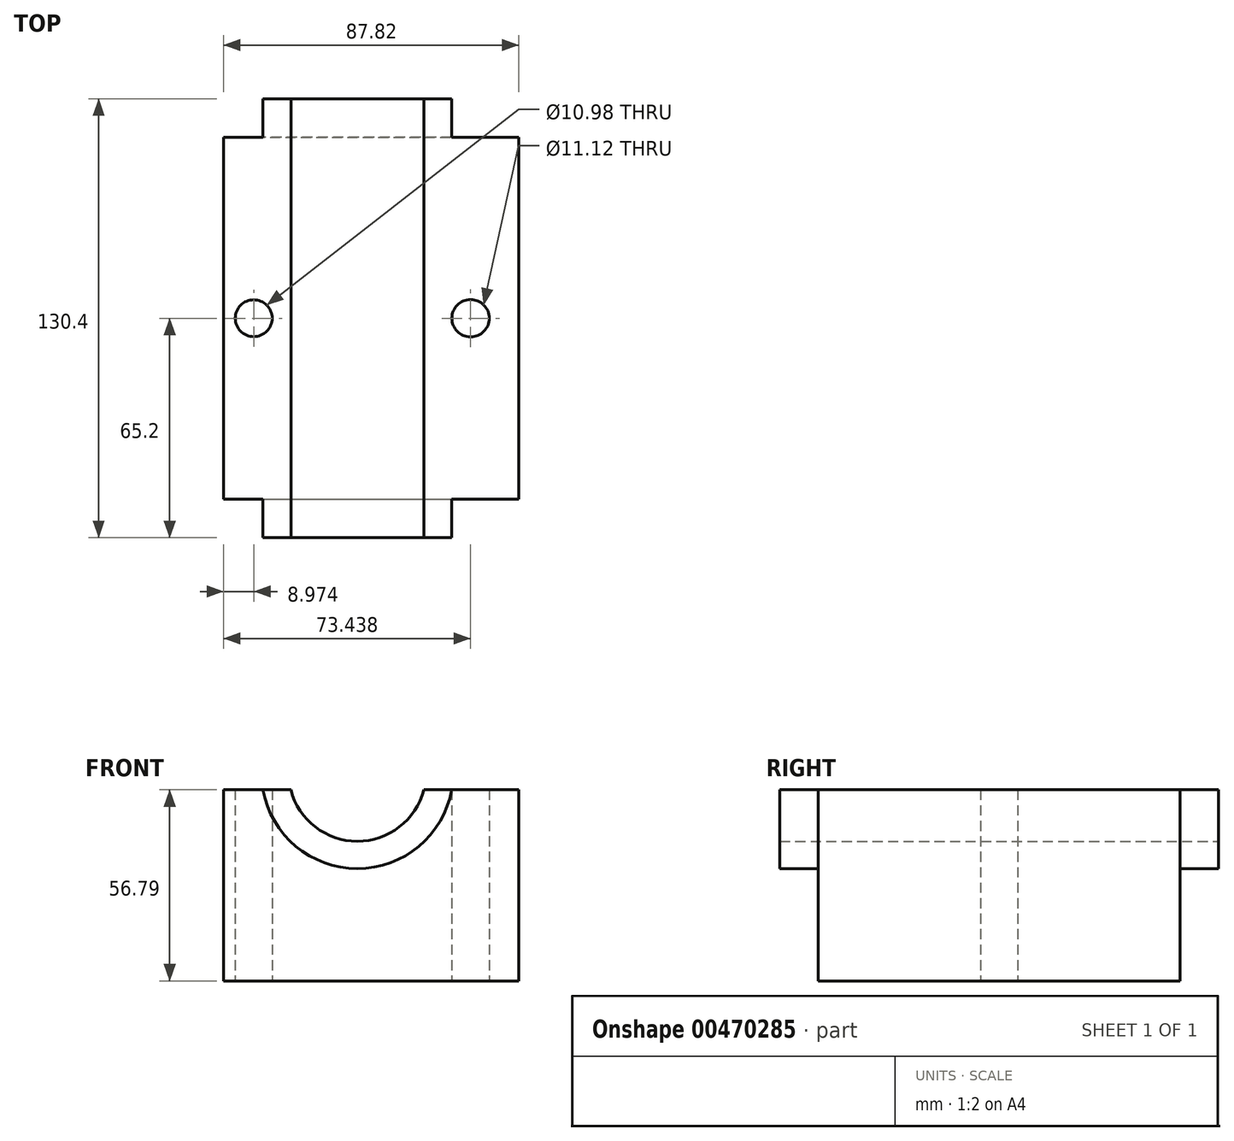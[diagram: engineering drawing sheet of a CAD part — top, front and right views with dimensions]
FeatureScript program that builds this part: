
annotation { "Feature Type Name" : "Feature", "Feature Type Description" : "" }
export const myFeature = defineFeature(function(context is Context, id is Id, definition is map)
    precondition{}
    {
        {
            var Q0;
            Q0=qCreatedBy(makeId("Top.planeOp"),FACE);
            var sketch = newSketch(context, id + "F0", { "sketchPlane" : qUnion([Q0])});
            skLineSegment(sketch, "E0.bottom", {"start": v(-39.78, -39.8) * mm, "end": v(48.04, -39.8) * mm});
            skLineSegment(sketch, "E0.top", {"start": v(-39.78, 53.76) * mm, "end": v(48.04, 53.76) * mm});
            skLineSegment(sketch, "E0.left", {"start": v(-39.78, -39.8) * mm, "end": v(-39.78, 53.76) * mm});
            skLineSegment(sketch, "E0.right", {"start": v(48.04, -39.8) * mm, "end": v(48.04, 53.76) * mm});
            skCircle(sketch, "E1", {"center": v(-32.67, 13.39) * mm, "radius": 4.61 * mm});
            skCircle(sketch, "E2", {"center": v(36.83, 13.39) * mm, "radius": 4.62 * mm});
            skSolve(sketch);
        }
        {
            var Q0;
            Q0=makeQuery(id+"F0.imprint","IMPRINT",FACE,{"disambiguationData":[TD([[makeQuery(id+"F0.imprint","IMPRINT",EDGE,{"derivedFrom":sQuery(id+"F0.wireOp",EDGE,"E0.bottom")}),1.0]])]});
            extrude(context, id + "F1", {"entities" : qUnion([Q0]), "depth" : 109.47 * mm});
        }
        {
            var Q0;
            Q0=makeQuery(id+"F1.opExtrude","SWEPT_FACE",FACE,{"disambiguationData":[OSD([sQuery(id+"F0.wireOp",EDGE,"E0.bottom")])]});
            var sketch = newSketch(context, id + "F2", { "sketchPlane" : qUnion([Q0])});
            skCircle(sketch, "E3", {"center": v(0, 61.9) * mm, "radius": 28.52 * mm});
            skCircle(sketch, "E4", {"center": v(0, 61.9) * mm, "radius": 20.41 * mm});
            skSolve(sketch);
        }
        {
            var Q0;
            Q0=makeQuery(id+"F2.imprint","IMPRINT",FACE,{"disambiguationData":[TD([[makeQuery(id+"F2.imprint","IMPRINT",EDGE,{"derivedFrom":sQuery(id+"F2.wireOp",EDGE,"E3")}),1.0]])]});
            extrude(context, id + "F3", {"entities" : qUnion([Q0]), "operationType" : NewBodyOperationType.ADD, "depth" : 25.4 * mm});
        }
        {
            var Q0;
            Q0=makeQuery(id+"F1.opExtrude","SWEPT_BODY",BODY,{"disambiguationData":[OSD([sQuery(id+"F0.wireOp",EDGE,"E0.bottom"),sQuery(id+"F0.wireOp",EDGE,"E0.top"),sQuery(id+"F0.wireOp",EDGE,"E0.left"),sQuery(id+"F0.wireOp",EDGE,"E0.right"),sQuery(id+"F0.wireOp",EDGE,"E1"),sQuery(id+"F0.wireOp",EDGE,"E2")])]});
            var Q1;
            Q1=qCreatedBy(makeId("Front.planeOp"),FACE);
            mirror(context, id + "F4", {"operationType" : NewBodyOperationType.ADD, "entities" : qUnion([Q0]), "mirrorPlane" : qUnion([Q1])});
        }
        {
            var Q0;
            Q0=qCreatedBy(makeId("Front.planeOp"),FACE);
            var sketch = newSketch(context, id + "F5", { "sketchPlane" : qUnion([Q0])});
            skLineSegment(sketch, "E5.bottom", {"start": v(-60.76, 117.68) * mm, "end": v(78.23, 117.68) * mm});
            skLineSegment(sketch, "E5.top", {"start": v(-60.76, 56.79) * mm, "end": v(78.23, 56.79) * mm});
            skLineSegment(sketch, "E5.left", {"start": v(-60.76, 117.68) * mm, "end": v(-60.76, 56.79) * mm});
            skLineSegment(sketch, "E5.right", {"start": v(78.23, 117.68) * mm, "end": v(78.23, 56.79) * mm});
            skSolve(sketch);
        }
        {
            var Q0;
            Q0=makeQuery(id+"F5.imprint","IMPRINT",FACE,{"disambiguationData":[TD([[makeQuery(id+"F5.imprint","IMPRINT",EDGE,{"derivedFrom":sQuery(id+"F5.wireOp",EDGE,"E5.bottom")}),-1.0]])]});
            extrude(context, id + "F6", {"entities" : qUnion([Q0]), "operationType" : NewBodyOperationType.REMOVE, "endBound" : BoundingType.SYMMETRIC, "depth" : 152.4 * mm});
        }
        {
            var Q0;
            Q0=makeQuery(id+"F4.boolean.opBoolean","SPLIT",FACE,{"disambiguationData":[TD([makeQuery(id+"F3.opExtrude","SWEPT_FACE",FACE,{"disambiguationData":[OSD([sQuery(id+"F2.wireOp",EDGE,"E4")])]})])],"derivedFrom":makeQuery(id+"F4.opPattern","COPY",FACE,{"derivedFrom":makeQuery(id+"F1.opExtrude","SWEPT_FACE",FACE,{"disambiguationData":[OSD([sQuery(id+"F0.wireOp",EDGE,"E0.top")])]}),"instanceName":"1"})});
            extrude(context, id + "F7", {"entities" : qUnion([Q0]), "operationType" : NewBodyOperationType.REMOVE, "endBound" : BoundingType.THROUGH_ALL, "oppositeDirection" : true, "depth" : 25.4 * mm});
        }
        {
            var Q0;
            Q0=qCreatedBy(makeId("Top.planeOp"),FACE);
            var sketch = newSketch(context, id + "F8", { "sketchPlane" : qUnion([Q0])});
            skCircle(sketch, "E6", {"center": v(-30.8, 0) * mm, "radius": 5.49 * mm});
            skCircle(sketch, "E7", {"center": v(33.66, 0) * mm, "radius": 5.56 * mm});
            skSolve(sketch);
        }
        {
            var Q0;
            Q0=makeQuery(id+"F8.imprint","IMPRINT",FACE,{"disambiguationData":[TD([[makeQuery(id+"F8.imprint","IMPRINT",EDGE,{"derivedFrom":sQuery(id+"F8.wireOp",EDGE,"E7")}),1.0]])]});
            var Q1;
            Q1=makeQuery(id+"F8.imprint","IMPRINT",FACE,{"disambiguationData":[TD([[makeQuery(id+"F8.imprint","IMPRINT",EDGE,{"derivedFrom":sQuery(id+"F8.wireOp",EDGE,"E6")}),1.0]])]});
            var Q2;
            Q2=sQuery(id+"F8.wireOp",EDGE,"E6");
            var Q3;
            Q3=sQuery(id+"F8.wireOp",EDGE,"E7");
            extrude(context, id + "F9", {"entities" : qUnion([Q0, Q1]), "operationType" : NewBodyOperationType.REMOVE, "surfaceEntities" : qUnion([Q2, Q3]), "endBound" : BoundingType.THROUGH_ALL, "depth" : 25.4 * mm});
        }
    });
